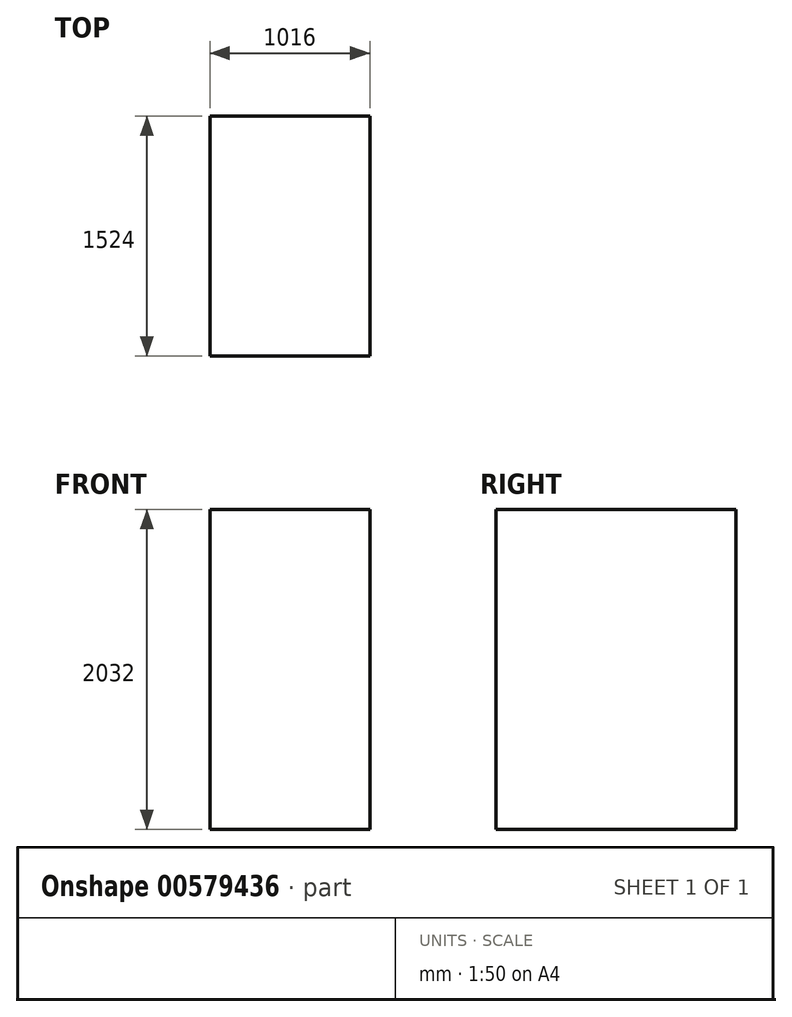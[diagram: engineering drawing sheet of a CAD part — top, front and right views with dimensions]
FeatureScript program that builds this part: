
annotation { "Feature Type Name" : "Feature", "Feature Type Description" : "" }
export const myFeature = defineFeature(function(context is Context, id is Id, definition is map)
    precondition{}
    {
        {
            var Q0;
            Q0=qCreatedBy(makeId("Top.planeOp"),FACE);
            var sketch = newSketch(context, id + "F0", { "sketchPlane" : qUnion([Q0])});
            skLineSegment(sketch, "E0.bottom", {"start": v(-1034.05, 1517.68) * mm, "end": v(-18.05, 1517.68) * mm});
            skLineSegment(sketch, "E0.top", {"start": v(-1034.05, -6.32) * mm, "end": v(-18.05, -6.32) * mm});
            skLineSegment(sketch, "E0.left", {"start": v(-1034.05, 1517.68) * mm, "end": v(-1034.05, -6.32) * mm});
            skLineSegment(sketch, "E0.right", {"start": v(-18.05, 1517.68) * mm, "end": v(-18.05, -6.32) * mm});
            skSolve(sketch);
        }
        {
            var Q0;
            Q0 = qSketchRegion(id + "F0", true);
            extrude(context, id + "F1", {"entities" : qUnion([Q0]), "depth" : 2032 * mm, "offsetDistance" : 25.4 * mm});
        }
    });
